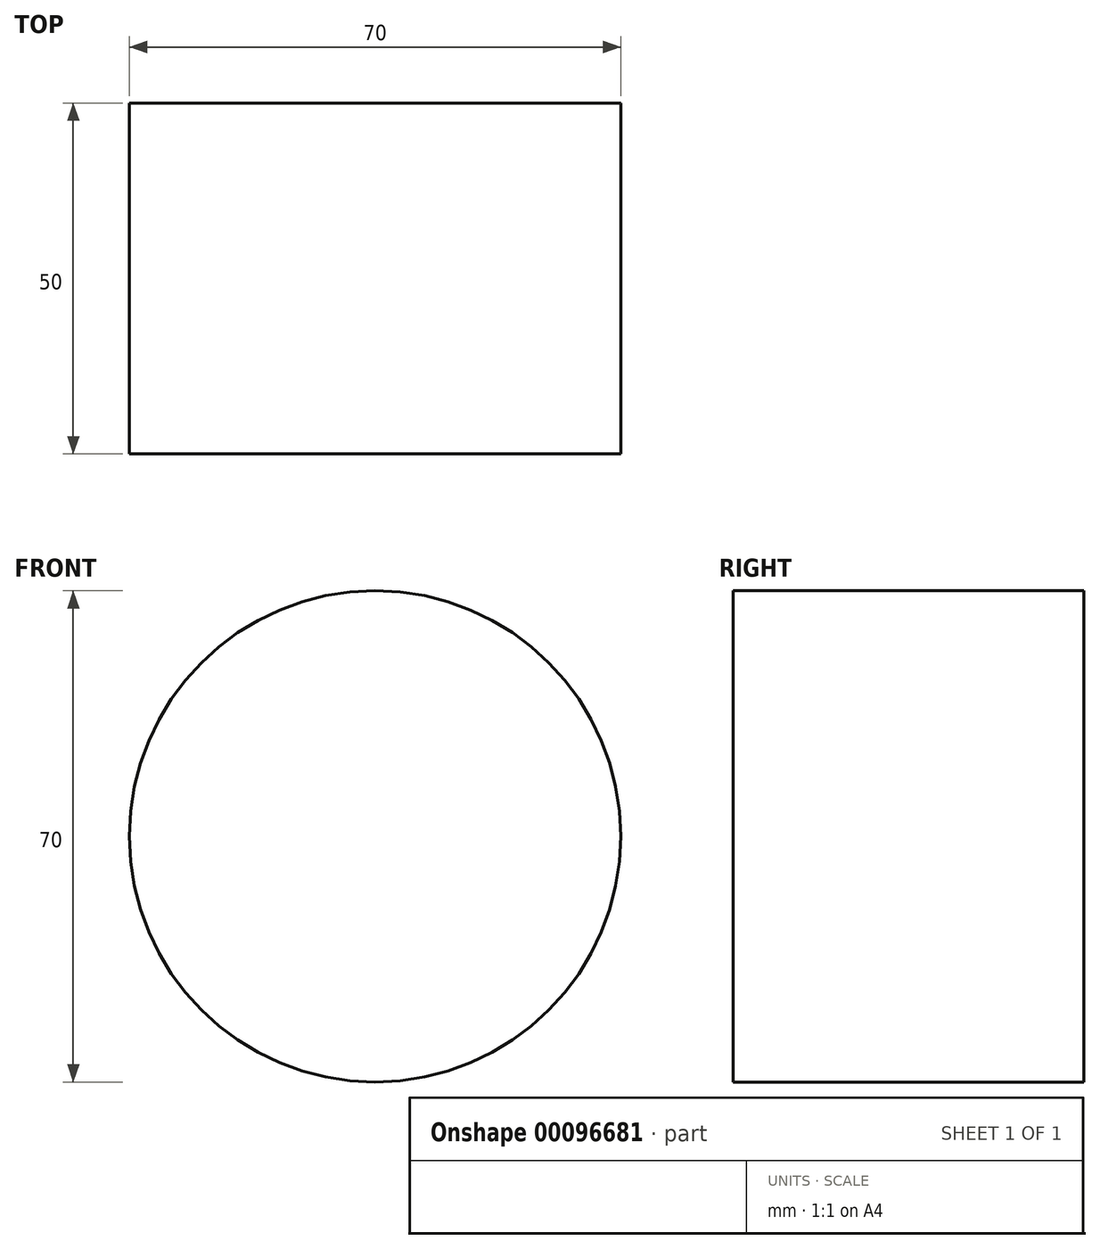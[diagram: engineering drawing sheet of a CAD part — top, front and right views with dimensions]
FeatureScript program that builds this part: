
annotation { "Feature Type Name" : "Feature", "Feature Type Description" : "" }
export const myFeature = defineFeature(function(context is Context, id is Id, definition is map)
    precondition{}
    {
        {
            var Q0;
            Q0=qCreatedBy(makeId("Front.planeOp"),FACE);
            var sketch = newSketch(context, id + "F0", { "sketchPlane" : qUnion([Q0])});
            skCircle(sketch, "E0", {"center": v(0, 0) * mm, "radius": 35 * mm});
            skSolve(sketch);
        }
        {
            var Q0;
            Q0 = qSketchRegion(id + "F0", true);
            extrude(context, id + "F1", {"entities" : qUnion([Q0]), "depth" : 50 * mm});
        }
    });
